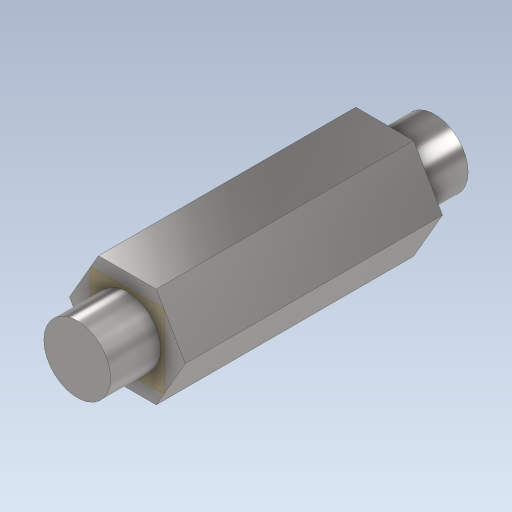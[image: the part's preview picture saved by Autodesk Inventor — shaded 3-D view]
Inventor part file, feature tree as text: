
AUTODESK INVENTOR PART (.ipt)
format: ipt  version: 2023 (Build 270158000, 158)  size: 319,488 bytes
history: native  units: in
note: dims shown in document units (in); Inventor stores cm internally (conversion verified against a paired STEP export)
features: other x3, sketch x2, plane x1, extrude x1
ambient origin geometry x8: Origin, YZ Plane, XZ Plane, XY Plane, X Axis, Y Axis, Z Axis, Center Point
bodies: Solid1 (feature_tree)
feature tree (7):
  other  "CH-1-01-0.25x1.875SmoothShaft.ipt"
  plane  "Work Plane1"
  extrude  "Extrusion1"  [1 undecoded]
  other  "Solid1::CH-1-01-0.25x1.875SmoothShaft.ipt"
  other  "TaggingFeature1"
  sketch  "Sketch1"  dims[d0=0.3937in d1=-0.1875in]
  sketch  "Sketch2"  dims[d2=0.375in d3=0.9636in d4=0.0in]
note: 1 required parameter value undecoded (feature->parameter linkage not recoverable at this tier; creation-order binding heuristic only, values carry confidence <= 0.55)
